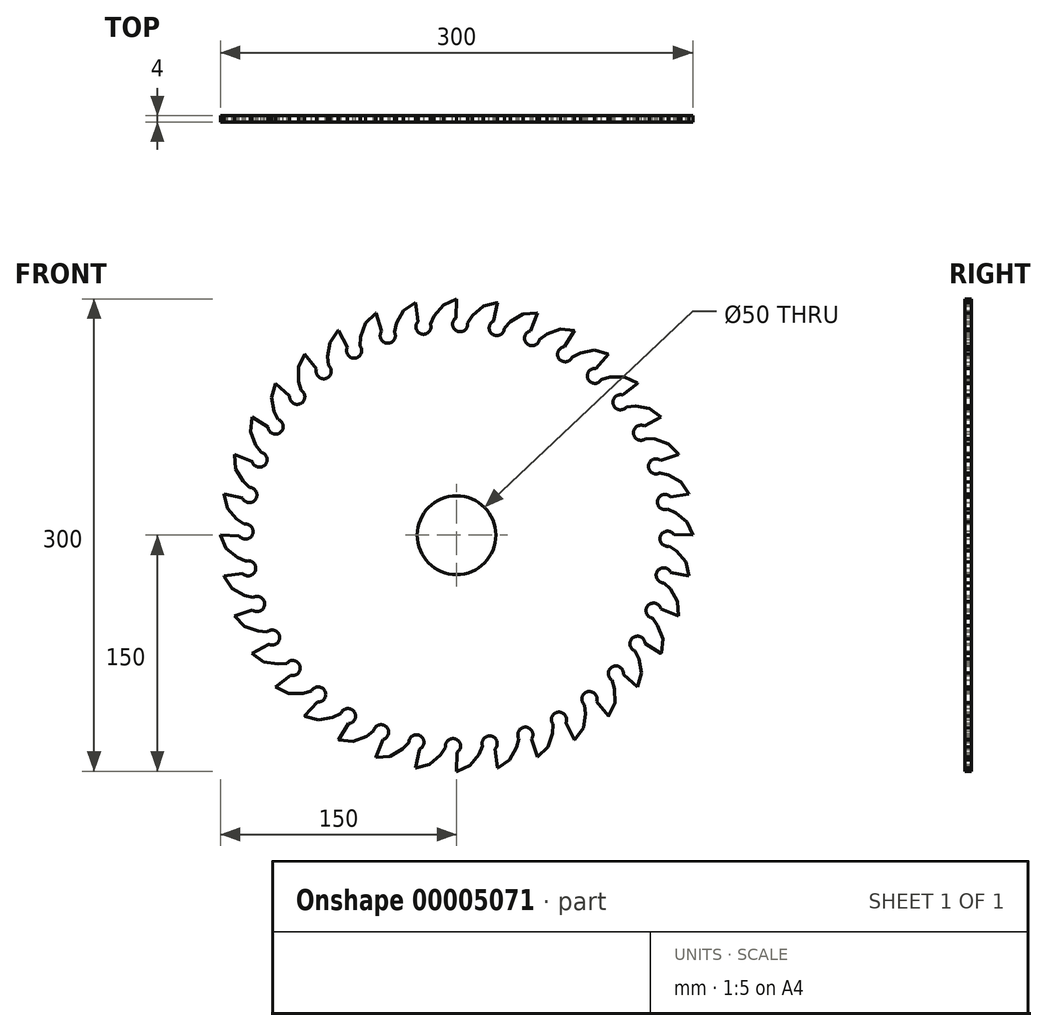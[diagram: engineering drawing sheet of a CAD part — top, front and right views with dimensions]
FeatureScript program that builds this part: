
annotation { "Feature Type Name" : "Feature", "Feature Type Description" : "" }
export const myFeature = defineFeature(function(context is Context, id is Id, definition is map)
    precondition{}
    {
        {
            var Q0;
            Q0=qCreatedBy(makeId("Front.planeOp"),FACE);
            var sketch = newSketch(context, id + "F0", { "sketchPlane" : qUnion([Q0])});
            skArc(sketch, "E0", {"start": v(0, 150) * mm, "mid": v(-13, -149.44) * mm, "end": v(25.9, 147.75) * mm});
            skLineSegment(sketch, "E1", {"start": v(0, 0) * mm, "end": v(0, 182.22) * mm, "construction": true});
            skLineSegment(sketch, "E2", {"start": v(0, 150) * mm, "end": v(-0.4, 138) * mm});
            skArc(sketch, "E3", {"start": v(-0.4, 138) * mm, "mid": v(0.39, 129.58) * mm, "end": v(7, 134.85) * mm});
            skLineSegment(sketch, "E4", {"start": v(7, 134.85) * mm, "end": v(10.19, 139.61) * mm});
            skLineSegment(sketch, "E5", {"start": v(10.19, 139.61) * mm, "end": v(17.1, 145.56) * mm});
            skLineSegment(sketch, "E6", {"start": v(17.1, 145.56) * mm, "end": v(25.9, 147.75) * mm});
            skSolve(sketch);
        }
        {
            var Q0;
            Q0=qSketchRegion(id+"F0",true);
            extrude(context, id + "F1", {"entities" : qUnion([Q0]), "depth" : 4 * mm});
        }
        {
            var Q0;
            Q0=makeQuery(id+"F1.opExtrude","SWEPT_FACE",FACE,{"disambiguationData":[OSD([sQuery(id+"F0.wireOp",EDGE,"E6")])]});
            var Q1;
            Q1=makeQuery(id+"F1.opExtrude","SWEPT_FACE",FACE,{"disambiguationData":[OSD([sQuery(id+"F0.wireOp",EDGE,"E5")])]});
            var Q2;
            Q2=makeQuery(id+"F1.opExtrude","SWEPT_FACE",FACE,{"disambiguationData":[OSD([sQuery(id+"F0.wireOp",EDGE,"E4")])]});
            var Q3;
            Q3=makeQuery(id+"F1.opExtrude","SWEPT_FACE",FACE,{"disambiguationData":[OSD([sQuery(id+"F0.wireOp",EDGE,"E3")])]});
            var Q4;
            Q4=makeQuery(id+"F1.opExtrude","SWEPT_FACE",FACE,{"disambiguationData":[OSD([sQuery(id+"F0.wireOp",EDGE,"E2")])]});
            var Q5;
            Q5=makeQuery(id+"F1.opExtrude","CAP_EDGE",EDGE,{"disambiguationData":[OSD([sQuery(id+"F0.wireOp",EDGE,"E0")])],"isStart":false});
            circularPattern(context, id + "F2", {"faces" : qUnion([Q0, Q1, Q2, Q3, Q4]), "axis" : qUnion([Q5]), "angle" : 10 * degree, "instanceCount" : round(36), "oppositeDirection" : true, "patternType" : PatternType.FACE});
        }
        {
            var Q0;
            Q0=makeQuery(id+"F1.opExtrude","CAP_FACE",FACE,{"disambiguationData":[OSD([sQuery(id+"F0.wireOp",EDGE,"E0"),sQuery(id+"F0.wireOp",EDGE,"E2"),sQuery(id+"F0.wireOp",EDGE,"E3"),sQuery(id+"F0.wireOp",EDGE,"E4"),sQuery(id+"F0.wireOp",EDGE,"E5"),sQuery(id+"F0.wireOp",EDGE,"E6")])],"isStart":false});
            var sketch = newSketch(context, id + "F3", { "sketchPlane" : qUnion([Q0])});
            skCircle(sketch, "E7", {"center": v(0, 0) * mm, "radius": 25 * mm});
            skSolve(sketch);
        }
        {
            var Q0;
            Q0=qSketchRegion(id+"F3",true);
            extrude(context, id + "F4", {"entities" : qUnion([Q0]), "operationType" : NewBodyOperationType.REMOVE, "endBound" : BoundingType.THROUGH_ALL, "oppositeDirection" : true, "depth" : 25 * mm});
        }
    });
